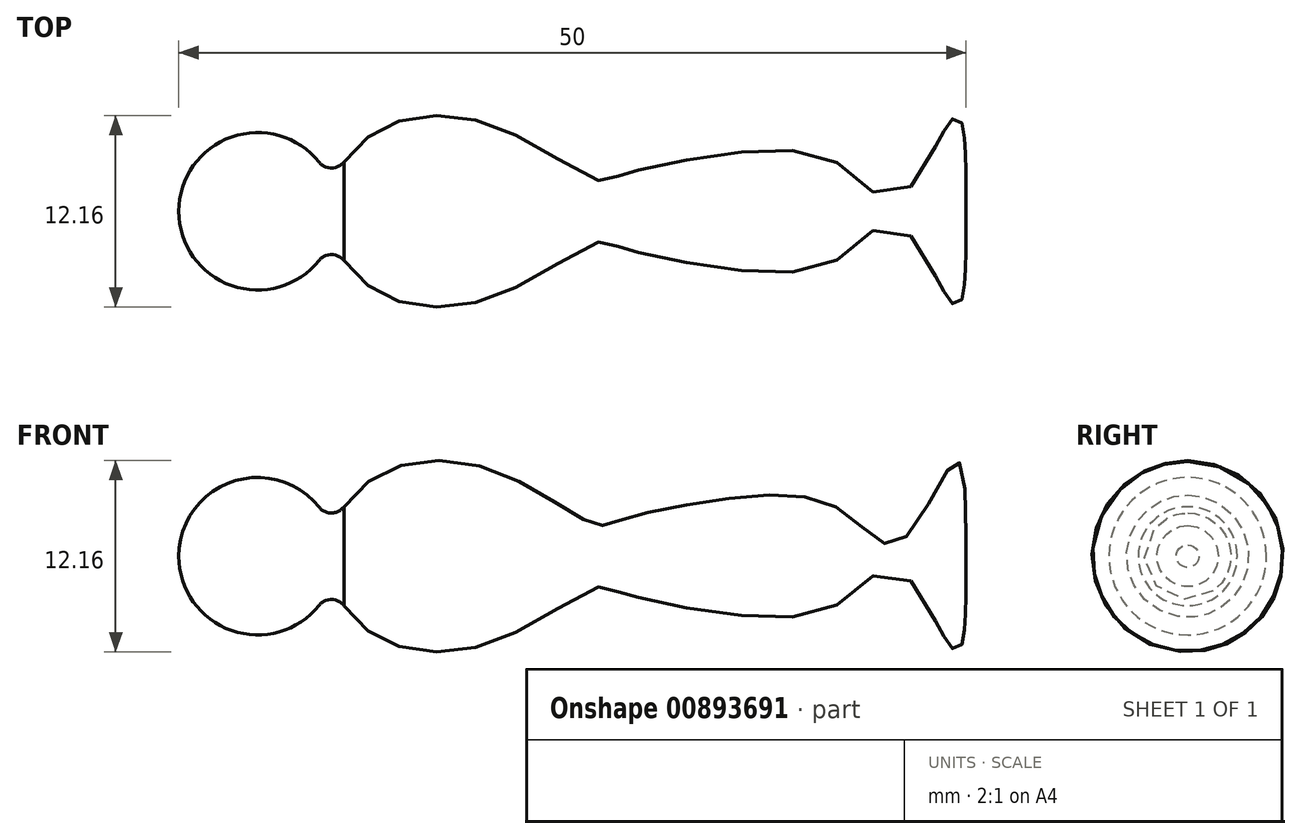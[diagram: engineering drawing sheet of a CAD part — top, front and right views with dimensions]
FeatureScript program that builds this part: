
annotation { "Feature Type Name" : "Feature", "Feature Type Description" : "" }
export const myFeature = defineFeature(function(context is Context, id is Id, definition is map)
    precondition{}
    {
        {
            var Q0;
            Q0=qCreatedBy(makeId("Front.planeOp"),FACE);
            var sketch = newSketch(context, id + "F0", { "sketchPlane" : qUnion([Q0])});
            skLineSegment(sketch, "E0", {"start": v(-28.05, 0) * mm, "end": v(21.95, 0) * mm});
            skArc(sketch, "E1", {"start": v(-18.4, 1.86) * mm, "mid": v(-24, 4.9) * mm, "end": v(-28.05, 0) * mm});
            skFitSpline(sketch, "E2", {"points": [v(-19.13, 0.55) * mm, v(-15.66, 5) * mm, v(-7.72, 5.32) * mm, v(-1.6, 2) * mm, v(0, 2.3) * mm, v(7.78, 3.76) * mm, v(14.23, 2.79) * mm, v(17.65, 0.83) * mm, v(21.26, 6) * mm, v(21.95, 0) * mm], "startDerivative": vector(17.47, 32.43) * mm, "endDerivative": vector(-0.42, -80.8) * mm});
            skSolve(sketch);
        }
        {
            var Q0;
            {var subQ0=sQuery(id+"F0.wireOp",EDGE,"E1");Q0=makeQuery(id+"F0.imprint","IMPRINT",FACE,{"disambiguationData":[TD([[makeQuery(id+"F0.imprint","IMPRINT",EDGE,{"derivedFrom":subQ0}),1.0]])]});}
            var Q1;
            {var subQ0=sQuery(id+"F0.wireOp",EDGE,"E2");Q1=makeQuery(id+"F0.imprint","IMPRINT",FACE,{"disambiguationData":[TD([[makeQuery(id+"F0.imprint","IMPRINT",EDGE,{"derivedFrom":subQ0}),-1.0]])]});}
            var Q2;
            Q2=sQuery(id+"F0.wireOp",EDGE,"E0");
            revolve(context, id + "F1", {"surfaceOperationType" : NewSurfaceOperationType.NEW, "entities" : qUnion([Q0, Q1]), "axis" : qUnion([Q2]), "revolveType" : RevolveType.FULL});
        }
        {
            var Q0;
            Q0=makeQuery(id+"F1.opRevolve","SWEPT_EDGE",EDGE,{"disambiguationData":[OSD([sQuery(id+"F0.wireOp",EDGE,"E1"),sQuery(id+"F0.wireOp",EDGE,"E2")])]});
            fillet(context, id + "F2", {"entities" : qUnion([Q0]), "radius" : 1 * mm, "tangentPropagation" : true, "allowEdgeOverflow" : false});
        }
    });
